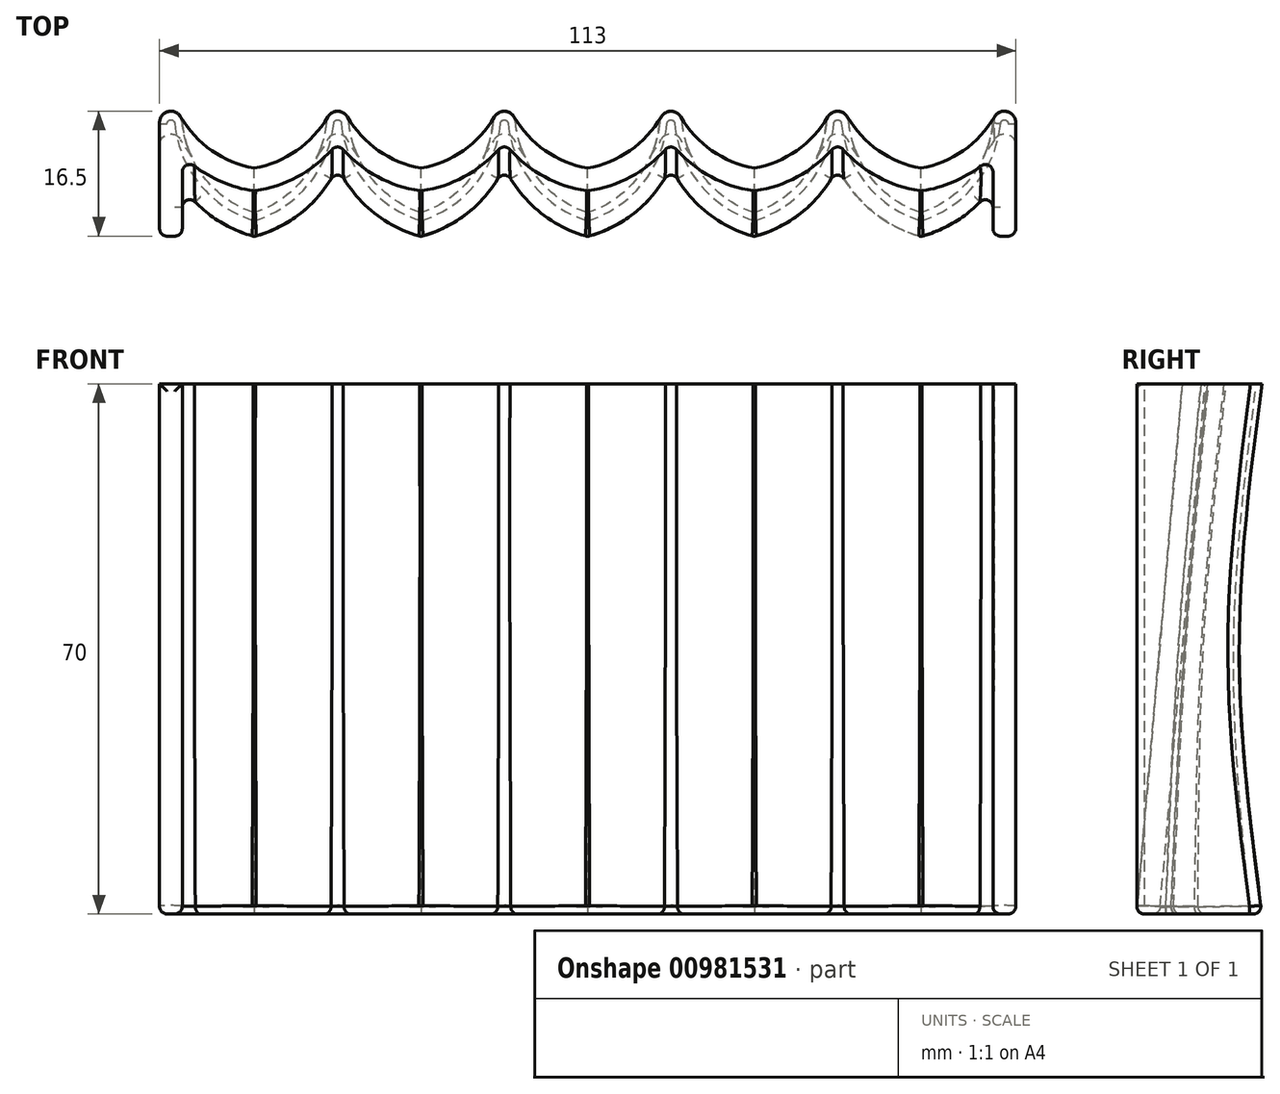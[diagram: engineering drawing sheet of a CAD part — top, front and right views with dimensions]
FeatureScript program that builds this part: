
annotation { "Feature Type Name" : "Feature", "Feature Type Description" : "" }
export const myFeature = defineFeature(function(context is Context, id is Id, definition is map)
    precondition{}
    {
        {
            var Q0;
            Q0=qCreatedBy(makeId("Top.planeOp"),FACE);
            var sketch = newSketch(context, id + "F0", { "sketchPlane" : qUnion([Q0])});
            skLineSegment(sketch, "E0", {"start": v(-56.5, 0) * mm, "end": v(-56.5, 15) * mm});
            skLineSegment(sketch, "E1", {"start": v(56.5, 0) * mm, "end": v(56.5, 15) * mm});
            skArc(sketch, "E2", {"start": v(-53.5, 15.12) * mm, "mid": v(-55.06, 16.5) * mm, "end": v(-56.5, 15) * mm});
            skLineSegment(sketch, "E3", {"start": v(-56.5, 0) * mm, "end": v(-53.5, 0) * mm});
            skLineSegment(sketch, "E4", {"start": v(-53.5, 0) * mm, "end": v(-53.5, 6.56) * mm});
            skLineSegment(sketch, "E5", {"start": v(56.5, 0) * mm, "end": v(53.5, 0) * mm});
            skLineSegment(sketch, "E6", {"start": v(53.5, 0) * mm, "end": v(53.5, 6.56) * mm});
            skLineSegment(sketch, "E7", {"start": v(-33, 3) * mm, "end": v(-11, 3) * mm, "construction": true});
            skLineSegment(sketch, "E8", {"start": v(-11, 3) * mm, "end": v(11, 3) * mm, "construction": true});
            skLineSegment(sketch, "E9", {"start": v(11, 3) * mm, "end": v(33, 3) * mm, "construction": true});
            skLineSegment(sketch, "E10", {"start": v(33, 3) * mm, "end": v(55, 3) * mm, "construction": true});
            skLineSegment(sketch, "E11", {"start": v(-33, 3) * mm, "end": v(-55, 3) * mm, "construction": true});
            skArc(sketch, "E12", {"start": v(56.5, 15) * mm, "mid": v(55, 16.5) * mm, "end": v(53.5, 15) * mm});
            skArc(sketch, "E13", {"start": v(-53.5, 15.12) * mm, "mid": v(-50.57, 7.64) * mm, "end": v(-44, 3) * mm});
            skArc(sketch, "E14", {"start": v(-31.5, 15.12) * mm, "mid": v(-33, 16.5) * mm, "end": v(-34.5, 15.12) * mm});
            skArc(sketch, "E15", {"start": v(-44, 3) * mm, "mid": v(-37.43, 7.64) * mm, "end": v(-34.5, 15.12) * mm});
            skLineSegment(sketch, "E16", {"start": v(0, 0) * mm, "end": v(0, 3) * mm, "construction": true});
            skArc(sketch, "E17", {"start": v(-31.5, 15.12) * mm, "mid": v(-28.57, 7.64) * mm, "end": v(-22, 3) * mm});
            skArc(sketch, "E18", {"start": v(-9.5, 15.12) * mm, "mid": v(-11, 16.5) * mm, "end": v(-12.5, 15.12) * mm});
            skArc(sketch, "E19", {"start": v(-22, 3) * mm, "mid": v(-15.43, 7.64) * mm, "end": v(-12.5, 15.12) * mm});
            skArc(sketch, "E20", {"start": v(-9.5, 15.12) * mm, "mid": v(-6.57, 7.64) * mm, "end": v(0, 3) * mm});
            skArc(sketch, "E21", {"start": v(0, 3) * mm, "mid": v(6.57, 7.64) * mm, "end": v(9.5, 15.12) * mm});
            skArc(sketch, "E22", {"start": v(12.5, 15.12) * mm, "mid": v(11, 16.5) * mm, "end": v(9.5, 15.12) * mm});
            skArc(sketch, "E23", {"start": v(12.5, 15.12) * mm, "mid": v(15.43, 7.64) * mm, "end": v(22, 3) * mm});
            skArc(sketch, "E24", {"start": v(22, 3) * mm, "mid": v(28.57, 7.64) * mm, "end": v(31.5, 15.12) * mm});
            skArc(sketch, "E25", {"start": v(34.5, 15.12) * mm, "mid": v(33, 16.5) * mm, "end": v(31.5, 15.12) * mm});
            skArc(sketch, "E26", {"start": v(34.5, 15.12) * mm, "mid": v(37.43, 7.64) * mm, "end": v(44, 3) * mm});
            skArc(sketch, "E27", {"start": v(44, 3) * mm, "mid": v(50.53, 7.59) * mm, "end": v(53.5, 15) * mm});
            skArc(sketch, "E28.0", {"start": v(44, -0.13) * mm, "mid": v(49.34, 2.37) * mm, "end": v(53.5, 6.56) * mm});
            skArc(sketch, "E28.1", {"start": v(33, 9.18) * mm, "mid": v(37.46, 3.3) * mm, "end": v(44, -0.13) * mm});
            skArc(sketch, "E28.2", {"start": v(22, -0.13) * mm, "mid": v(28.54, 3.3) * mm, "end": v(33, 9.18) * mm});
            skArc(sketch, "E28.3", {"start": v(11, 9.18) * mm, "mid": v(15.46, 3.3) * mm, "end": v(22, -0.13) * mm});
            skArc(sketch, "E28.4", {"start": v(0, -0.13) * mm, "mid": v(6.54, 3.3) * mm, "end": v(11, 9.18) * mm});
            skArc(sketch, "E28.5", {"start": v(-11, 9.18) * mm, "mid": v(-6.54, 3.3) * mm, "end": v(0, -0.13) * mm});
            skArc(sketch, "E28.6", {"start": v(-53.5, 6.56) * mm, "mid": v(-49.34, 2.37) * mm, "end": v(-44, -0.13) * mm});
            skArc(sketch, "E28.7", {"start": v(-44, -0.13) * mm, "mid": v(-37.46, 3.3) * mm, "end": v(-33, 9.18) * mm});
            skArc(sketch, "E28.8", {"start": v(-33, 9.18) * mm, "mid": v(-28.54, 3.3) * mm, "end": v(-22, -0.13) * mm});
            skArc(sketch, "E28.9", {"start": v(-22, -0.13) * mm, "mid": v(-15.46, 3.3) * mm, "end": v(-11, 9.18) * mm});
            skSolve(sketch);
        }
        {
            var Q0;
            Q0=qCreatedBy(makeId("Top.planeOp"),FACE);
            cPlane(context, id + "F1", {"entities" : qUnion([Q0]), "cplaneType" : CPlaneType.OFFSET, "offset" : 70 * mm, "width" : 150 * mm, "height" : 150 * mm});
        }
        {
            var Q0;
            Q0=qCreatedBy(id+"F1.planeOp",FACE);
            var sketch = newSketch(context, id + "F2", { "sketchPlane" : qUnion([Q0])});
            skLineSegment(sketch, "E29.0", {"start": v(-56.5, 0) * mm, "end": v(-53.5, 0) * mm});
            skLineSegment(sketch, "E30.0", {"start": v(56.5, 0) * mm, "end": v(53.5, 0) * mm});
            skLineSegment(sketch, "E31.0", {"start": v(56.5, 0) * mm, "end": v(56.5, 15) * mm});
            skLineSegment(sketch, "E32.0", {"start": v(-56.5, 0) * mm, "end": v(-56.5, 15) * mm});
            skLineSegment(sketch, "E33.0", {"start": v(-33, 3) * mm, "end": v(-55, 3) * mm, "construction": true});
            skLineSegment(sketch, "E34.0", {"start": v(-33, 3) * mm, "end": v(-11, 3) * mm, "construction": true});
            skLineSegment(sketch, "E35.0", {"start": v(-11, 3) * mm, "end": v(11, 3) * mm, "construction": true});
            skLineSegment(sketch, "E36.0", {"start": v(11, 3) * mm, "end": v(33, 3) * mm, "construction": true});
            skLineSegment(sketch, "E37.0", {"start": v(33, 3) * mm, "end": v(55, 3) * mm, "construction": true});
            skArc(sketch, "E38", {"start": v(-53.7, 15.75) * mm, "mid": v(-55.4, 16.45) * mm, "end": v(-56.5, 15) * mm});
            skLineSegment(sketch, "E39", {"start": v(-55, 9) * mm, "end": v(-33, 9) * mm, "construction": true});
            skLineSegment(sketch, "E40", {"start": v(-33, 9) * mm, "end": v(-11, 9) * mm, "construction": true});
            skLineSegment(sketch, "E41", {"start": v(-11, 9) * mm, "end": v(11, 9) * mm, "construction": true});
            skLineSegment(sketch, "E42", {"start": v(11, 9) * mm, "end": v(33, 9) * mm, "construction": true});
            skLineSegment(sketch, "E43", {"start": v(33, 9) * mm, "end": v(55, 9) * mm, "construction": true});
            skArc(sketch, "E44", {"start": v(-53.7, 15.75) * mm, "mid": v(-49.6, 11.3) * mm, "end": v(-44, 9) * mm});
            skArc(sketch, "E45", {"start": v(-44, 9) * mm, "mid": v(-38.4, 11.3) * mm, "end": v(-34.3, 15.75) * mm});
            skArc(sketch, "E46", {"start": v(-31.7, 15.75) * mm, "mid": v(-33, 16.5) * mm, "end": v(-34.3, 15.75) * mm});
            skArc(sketch, "E47", {"start": v(-31.7, 15.75) * mm, "mid": v(-27.6, 11.3) * mm, "end": v(-22, 9) * mm});
            skArc(sketch, "E48", {"start": v(-22, 9) * mm, "mid": v(-16.4, 11.3) * mm, "end": v(-12.3, 15.75) * mm});
            skArc(sketch, "E49", {"start": v(-9.7, 15.75) * mm, "mid": v(-11, 16.5) * mm, "end": v(-12.3, 15.75) * mm});
            skArc(sketch, "E50", {"start": v(-9.7, 15.75) * mm, "mid": v(-5.6, 11.3) * mm, "end": v(0, 9) * mm});
            skArc(sketch, "E51", {"start": v(0, 9) * mm, "mid": v(5.6, 11.3) * mm, "end": v(9.7, 15.75) * mm});
            skArc(sketch, "E52", {"start": v(12.3, 15.75) * mm, "mid": v(11, 16.5) * mm, "end": v(9.7, 15.75) * mm});
            skArc(sketch, "E53", {"start": v(12.3, 15.75) * mm, "mid": v(16.4, 11.3) * mm, "end": v(22, 9) * mm});
            skArc(sketch, "E54", {"start": v(22, 9) * mm, "mid": v(27.6, 11.3) * mm, "end": v(31.7, 15.75) * mm});
            skArc(sketch, "E55", {"start": v(34.3, 15.75) * mm, "mid": v(33, 16.5) * mm, "end": v(31.7, 15.75) * mm});
            skArc(sketch, "E56", {"start": v(34.3, 15.75) * mm, "mid": v(38.4, 11.3) * mm, "end": v(44, 9) * mm});
            skArc(sketch, "E57", {"start": v(44, 9) * mm, "mid": v(49.6, 11.3) * mm, "end": v(53.7, 15.75) * mm});
            skArc(sketch, "E58", {"start": v(56.5, 15) * mm, "mid": v(55.4, 16.45) * mm, "end": v(53.7, 15.75) * mm});
            skArc(sketch, "E59.0", {"start": v(44, 5.96) * mm, "mid": v(49.12, 7.55) * mm, "end": v(53.5, 10.65) * mm});
            skArc(sketch, "E59.1", {"start": v(33, 12.33) * mm, "mid": v(37.88, 8.08) * mm, "end": v(44, 5.96) * mm});
            skArc(sketch, "E59.2", {"start": v(22, 5.96) * mm, "mid": v(28.12, 8.08) * mm, "end": v(33, 12.33) * mm});
            skArc(sketch, "E59.3", {"start": v(11, 12.33) * mm, "mid": v(15.88, 8.08) * mm, "end": v(22, 5.96) * mm});
            skArc(sketch, "E59.4", {"start": v(0, 5.96) * mm, "mid": v(6.12, 8.08) * mm, "end": v(11, 12.33) * mm});
            skArc(sketch, "E59.5", {"start": v(-11, 12.33) * mm, "mid": v(-6.12, 8.08) * mm, "end": v(0, 5.96) * mm});
            skArc(sketch, "E59.6", {"start": v(-53.5, 10.65) * mm, "mid": v(-49.12, 7.55) * mm, "end": v(-44, 5.96) * mm});
            skArc(sketch, "E59.7", {"start": v(-44, 5.96) * mm, "mid": v(-37.88, 8.08) * mm, "end": v(-33, 12.33) * mm});
            skArc(sketch, "E59.8", {"start": v(-33, 12.33) * mm, "mid": v(-28.12, 8.08) * mm, "end": v(-22, 5.96) * mm});
            skArc(sketch, "E59.9", {"start": v(-22, 5.96) * mm, "mid": v(-15.88, 8.08) * mm, "end": v(-11, 12.33) * mm});
            skLineSegment(sketch, "E60", {"start": v(-53.5, 10.65) * mm, "end": v(-53.5, 0) * mm});
            skLineSegment(sketch, "E61", {"start": v(53.5, 10.65) * mm, "end": v(53.5, 0) * mm});
            skSolve(sketch);
        }
        {
            var Q0;
            Q0=qCreatedBy(makeId("Top.planeOp"),FACE);
            cPlane(context, id + "F3", {"entities" : qUnion([Q0]), "cplaneType" : CPlaneType.OFFSET, "offset" : 35 * mm, "width" : 150 * mm, "height" : 150 * mm});
        }
        {
            var Q0;
            Q0=qCreatedBy(id+"F3.planeOp",FACE);
            var sketch = newSketch(context, id + "F4", { "sketchPlane" : qUnion([Q0])});
            skLineSegment(sketch, "E62.0", {"start": v(-33, 3) * mm, "end": v(-55, 3) * mm, "construction": true});
            skLineSegment(sketch, "E63.0", {"start": v(-33, 3) * mm, "end": v(-11, 3) * mm, "construction": true});
            skLineSegment(sketch, "E64.0", {"start": v(-11, 3) * mm, "end": v(11, 3) * mm, "construction": true});
            skLineSegment(sketch, "E65.0", {"start": v(11, 3) * mm, "end": v(33, 3) * mm, "construction": true});
            skLineSegment(sketch, "E66.0", {"start": v(33, 3) * mm, "end": v(55, 3) * mm, "construction": true});
            skLineSegment(sketch, "E67.0", {"start": v(33, 9) * mm, "end": v(55, 9) * mm, "construction": true});
            skLineSegment(sketch, "E68.0", {"start": v(11, 9) * mm, "end": v(33, 9) * mm, "construction": true});
            skLineSegment(sketch, "E69.0", {"start": v(-11, 9) * mm, "end": v(11, 9) * mm, "construction": true});
            skLineSegment(sketch, "E70.0", {"start": v(-33, 9) * mm, "end": v(-11, 9) * mm, "construction": true});
            skLineSegment(sketch, "E71.0", {"start": v(-55, 9) * mm, "end": v(-33, 9) * mm, "construction": true});
            skLineSegment(sketch, "E72.0", {"start": v(-56.5, 0) * mm, "end": v(-53.5, 0) * mm});
            skLineSegment(sketch, "E73.0", {"start": v(-56.5, 0) * mm, "end": v(-56.5, 15) * mm, "construction": true});
            skLineSegment(sketch, "E74.0", {"start": v(56.5, 0) * mm, "end": v(53.5, 0) * mm});
            skLineSegment(sketch, "E75.0", {"start": v(56.5, 0) * mm, "end": v(56.5, 15) * mm, "construction": true});
            skLineSegment(sketch, "E76", {"start": v(-55, 6) * mm, "end": v(-33, 6) * mm, "construction": true});
            skLineSegment(sketch, "E77", {"start": v(-33, 6) * mm, "end": v(-11, 6) * mm, "construction": true});
            skLineSegment(sketch, "E78", {"start": v(-11, 6) * mm, "end": v(11, 6) * mm, "construction": true});
            skLineSegment(sketch, "E79", {"start": v(11, 6) * mm, "end": v(33, 6) * mm, "construction": true});
            skLineSegment(sketch, "E80", {"start": v(33, 6) * mm, "end": v(55, 6) * mm, "construction": true});
            skLineSegment(sketch, "E81", {"start": v(-56.5, 0) * mm, "end": v(-56.5, 12) * mm});
            skLineSegment(sketch, "E82", {"start": v(56.5, 0) * mm, "end": v(56.5, 12) * mm});
            skArc(sketch, "E83", {"start": v(-53.7, 12.75) * mm, "mid": v(-55.4, 13.45) * mm, "end": v(-56.5, 12) * mm});
            skArc(sketch, "E84", {"start": v(-53.7, 12.75) * mm, "mid": v(-49.6, 8.3) * mm, "end": v(-44, 6) * mm});
            skArc(sketch, "E85", {"start": v(-44, 6) * mm, "mid": v(-38.4, 8.3) * mm, "end": v(-34.3, 12.75) * mm});
            skArc(sketch, "E86", {"start": v(-31.7, 12.75) * mm, "mid": v(-33, 13.5) * mm, "end": v(-34.3, 12.75) * mm});
            skArc(sketch, "E87", {"start": v(-31.7, 12.75) * mm, "mid": v(-27.6, 8.3) * mm, "end": v(-22, 6) * mm});
            skArc(sketch, "E88", {"start": v(-22, 6) * mm, "mid": v(-16.4, 8.3) * mm, "end": v(-12.3, 12.75) * mm});
            skArc(sketch, "E89", {"start": v(-9.7, 12.75) * mm, "mid": v(-11, 13.5) * mm, "end": v(-12.3, 12.75) * mm});
            skArc(sketch, "E90", {"start": v(-9.7, 12.75) * mm, "mid": v(-5.6, 8.3) * mm, "end": v(0, 6) * mm});
            skArc(sketch, "E91", {"start": v(0, 6) * mm, "mid": v(5.6, 8.3) * mm, "end": v(9.7, 12.75) * mm});
            skArc(sketch, "E92", {"start": v(12.3, 12.75) * mm, "mid": v(11, 13.5) * mm, "end": v(9.7, 12.75) * mm});
            skArc(sketch, "E93", {"start": v(12.3, 12.75) * mm, "mid": v(16.4, 8.3) * mm, "end": v(22, 6) * mm});
            skArc(sketch, "E94", {"start": v(22, 6) * mm, "mid": v(27.6, 8.3) * mm, "end": v(31.7, 12.75) * mm});
            skArc(sketch, "E95", {"start": v(34.3, 12.75) * mm, "mid": v(33, 13.5) * mm, "end": v(31.7, 12.75) * mm});
            skArc(sketch, "E96", {"start": v(34.3, 12.75) * mm, "mid": v(38.4, 8.3) * mm, "end": v(44, 6) * mm});
            skArc(sketch, "E97", {"start": v(44, 6) * mm, "mid": v(49.6, 8.3) * mm, "end": v(53.7, 12.75) * mm});
            skLineSegment(sketch, "E98", {"start": v(53.5, 7.65) * mm, "end": v(53.5, 0) * mm});
            skLineSegment(sketch, "E99", {"start": v(-53.5, 7.65) * mm, "end": v(-53.5, 0) * mm});
            skLineSegment(sketch, "E100", {"start": v(0, 6) * mm, "end": v(0, 3) * mm, "construction": true});
            skLineSegment(sketch, "E101", {"start": v(0, 3) * mm, "end": v(0, 6) * mm, "construction": true});
            skLineSegment(sketch, "E102", {"start": v(0, 6) * mm, "end": v(0, 9) * mm, "construction": true});
            skArc(sketch, "E103", {"start": v(56.5, 12) * mm, "mid": v(55.4, 13.45) * mm, "end": v(53.7, 12.75) * mm});
            skArc(sketch, "E104.0", {"start": v(44, 2.96) * mm, "mid": v(49.12, 4.55) * mm, "end": v(53.5, 7.65) * mm});
            skArc(sketch, "E104.1", {"start": v(33, 9.33) * mm, "mid": v(37.88, 5.08) * mm, "end": v(44, 2.96) * mm});
            skArc(sketch, "E104.2", {"start": v(22, 2.96) * mm, "mid": v(28.12, 5.08) * mm, "end": v(33, 9.33) * mm});
            skArc(sketch, "E104.3", {"start": v(11, 9.33) * mm, "mid": v(15.88, 5.08) * mm, "end": v(22, 2.96) * mm});
            skArc(sketch, "E104.4", {"start": v(0, 2.96) * mm, "mid": v(6.12, 5.08) * mm, "end": v(11, 9.33) * mm});
            skArc(sketch, "E104.5", {"start": v(-11, 9.33) * mm, "mid": v(-6.12, 5.08) * mm, "end": v(0, 2.96) * mm});
            skArc(sketch, "E104.6", {"start": v(-53.5, 7.65) * mm, "mid": v(-49.12, 4.55) * mm, "end": v(-44, 2.96) * mm});
            skArc(sketch, "E104.7", {"start": v(-44, 2.96) * mm, "mid": v(-37.88, 5.08) * mm, "end": v(-33, 9.33) * mm});
            skArc(sketch, "E104.8", {"start": v(-33, 9.33) * mm, "mid": v(-28.12, 5.08) * mm, "end": v(-22, 2.96) * mm});
            skArc(sketch, "E104.9", {"start": v(-22, 2.96) * mm, "mid": v(-15.88, 5.08) * mm, "end": v(-11, 9.33) * mm});
            skSolve(sketch);
        }
        {
            var Q0;
            Q0 = qSketchRegion(id + "F0", true);
            var Q1;
            Q1 = qSketchRegion(id + "F4", true);
            var Q2;
            Q2 = qSketchRegion(id + "F2", true);
            loft(context, id + "F5", {"sheetProfilesArray" : [{ "sheetProfileEntities" : qUnion([Q0]) }, { "sheetProfileEntities" : qUnion([Q1]) }, { "sheetProfileEntities" : qUnion([Q2]) }]});
        }
        {
            var Q0;
            Q0=makeQuery(id+"F5.opLoft","CAP_FACE",FACE,{"disambiguationData":[OSD([makeQuery(id+"F0.imprint","IMPRINT",FACE,{"disambiguationData":[TD([[makeQuery(id+"F0.imprint","IMPRINT",EDGE,{"derivedFrom":sQuery(id+"F0.wireOp",EDGE,"E0")}),-1.0]])]})])],"isStart":true});
            var Q1;
            Q1=makeQuery(id+"F5.opLoft","SWEPT_EDGE",EDGE,{"disambiguationData":[OSD([sQuery(id+"F0.wireOp",EDGE,"E28.0"),sQuery(id+"F0.wireOp",EDGE,"E28.1"),sQuery(id+"F2.wireOp",EDGE,"E59.0"),sQuery(id+"F2.wireOp",EDGE,"E59.1"),sQuery(id+"F4.wireOp",EDGE,"f05942cf-1fd4-4216-8ab5-6da0ba2a5f30.0"),sQuery(id+"F4.wireOp",EDGE,"f05942cf-1fd4-4216-8ab5-6da0ba2a5f30.1")])]});
            var Q2;
            Q2=makeQuery(id+"F5.opLoft","SWEPT_EDGE",EDGE,{"disambiguationData":[OSD([sQuery(id+"F0.wireOp",EDGE,"E28.4"),sQuery(id+"F0.wireOp",EDGE,"E28.5"),sQuery(id+"F2.wireOp",EDGE,"E59.4"),sQuery(id+"F2.wireOp",EDGE,"E59.5"),sQuery(id+"F4.wireOp",EDGE,"f05942cf-1fd4-4216-8ab5-6da0ba2a5f30.4"),sQuery(id+"F4.wireOp",EDGE,"f05942cf-1fd4-4216-8ab5-6da0ba2a5f30.5")])]});
            var Q3;
            Q3=makeQuery(id+"F5.opLoft","SWEPT_EDGE",EDGE,{"disambiguationData":[OSD([sQuery(id+"F0.wireOp",EDGE,"E28.8"),sQuery(id+"F0.wireOp",EDGE,"E28.9"),sQuery(id+"F2.wireOp",EDGE,"E59.8"),sQuery(id+"F2.wireOp",EDGE,"E59.9"),sQuery(id+"F4.wireOp",EDGE,"f05942cf-1fd4-4216-8ab5-6da0ba2a5f30.8"),sQuery(id+"F4.wireOp",EDGE,"f05942cf-1fd4-4216-8ab5-6da0ba2a5f30.9")])]});
            var Q4;
            Q4=makeQuery(id+"F5.opLoft","SWEPT_EDGE",EDGE,{"disambiguationData":[OSD([sQuery(id+"F0.wireOp",EDGE,"E28.6"),sQuery(id+"F0.wireOp",EDGE,"E28.7"),sQuery(id+"F2.wireOp",EDGE,"E59.6"),sQuery(id+"F2.wireOp",EDGE,"E59.7"),sQuery(id+"F4.wireOp",EDGE,"f05942cf-1fd4-4216-8ab5-6da0ba2a5f30.6"),sQuery(id+"F4.wireOp",EDGE,"f05942cf-1fd4-4216-8ab5-6da0ba2a5f30.7")])]});
            var Q5;
            Q5=makeQuery(id+"F5.opLoft","SWEPT_FACE",FACE,{"disambiguationData":[OSD([sQuery(id+"F0.wireOp",EDGE,"E0"),sQuery(id+"F0.wireOp",EDGE,"E3"),sQuery(id+"F0.wireOp",EDGE,"E4"),sQuery(id+"F2.wireOp",EDGE,"E29.0"),sQuery(id+"F2.wireOp",EDGE,"E32.0"),sQuery(id+"F2.wireOp",EDGE,"E60"),sQuery(id+"F4.wireOp",EDGE,"E72.0"),sQuery(id+"F4.wireOp",EDGE,"E81"),sQuery(id+"F4.wireOp",EDGE,"E99")])]});
            var Q6;
            Q6=makeQuery(id+"F5.opLoft","SWEPT_EDGE",EDGE,{"disambiguationData":[OSD([sQuery(id+"F0.wireOp",EDGE,"E0"),sQuery(id+"F0.wireOp",EDGE,"E3"),sQuery(id+"F2.wireOp",EDGE,"E29.0"),sQuery(id+"F2.wireOp",EDGE,"E32.0"),sQuery(id+"F4.wireOp",EDGE,"E72.0"),sQuery(id+"F4.wireOp",EDGE,"E81")])]});
            var Q7;
            Q7=makeQuery(id+"F5.opLoft","SWEPT_EDGE",EDGE,{"disambiguationData":[OSD([sQuery(id+"F0.wireOp",EDGE,"E1"),sQuery(id+"F0.wireOp",EDGE,"E5"),sQuery(id+"F2.wireOp",EDGE,"E30.0"),sQuery(id+"F2.wireOp",EDGE,"E31.0"),sQuery(id+"F4.wireOp",EDGE,"E74.0"),sQuery(id+"F4.wireOp",EDGE,"E82")])]});
            var Q8;
            Q8=makeQuery(id+"F5.opLoft","SWEPT_EDGE",EDGE,{"disambiguationData":[OSD([sQuery(id+"F0.wireOp",EDGE,"E5"),sQuery(id+"F0.wireOp",EDGE,"E6"),sQuery(id+"F2.wireOp",EDGE,"E30.0"),sQuery(id+"F2.wireOp",EDGE,"E61"),sQuery(id+"F4.wireOp",EDGE,"E74.0"),sQuery(id+"F4.wireOp",EDGE,"E98")])]});
            var Q9;
            Q9=makeQuery(id+"F5.opLoft","SWEPT_EDGE",EDGE,{"disambiguationData":[OSD([sQuery(id+"F0.wireOp",EDGE,"E28.2"),sQuery(id+"F0.wireOp",EDGE,"E28.3"),sQuery(id+"F2.wireOp",EDGE,"E59.2"),sQuery(id+"F2.wireOp",EDGE,"E59.3"),sQuery(id+"F4.wireOp",EDGE,"f05942cf-1fd4-4216-8ab5-6da0ba2a5f30.2"),sQuery(id+"F4.wireOp",EDGE,"f05942cf-1fd4-4216-8ab5-6da0ba2a5f30.3")])]});
            var Q10;
            Q10=makeQuery(id+"F5.opLoft","SWEPT_EDGE",EDGE,{"disambiguationData":[OSD([sQuery(id+"F0.wireOp",EDGE,"E6"),sQuery(id+"F0.wireOp",EDGE,"E28.0"),sQuery(id+"F2.wireOp",EDGE,"E59.0"),sQuery(id+"F2.wireOp",EDGE,"E61"),sQuery(id+"F4.wireOp",EDGE,"E98"),sQuery(id+"F4.wireOp",EDGE,"E104.0")])]});
            var Q11;
            Q11=makeQuery(id+"F5.opLoft","SWEPT_EDGE",EDGE,{"disambiguationData":[OSD([sQuery(id+"F0.wireOp",EDGE,"E4"),sQuery(id+"F0.wireOp",EDGE,"E28.6"),sQuery(id+"F2.wireOp",EDGE,"E59.6"),sQuery(id+"F2.wireOp",EDGE,"E60"),sQuery(id+"F4.wireOp",EDGE,"E99"),sQuery(id+"F4.wireOp",EDGE,"E104.6")])]});
            var Q12;
            Q12=makeQuery(id+"F5.opLoft","SWEPT_EDGE",EDGE,{"disambiguationData":[OSD([sQuery(id+"F0.wireOp",EDGE,"E28.7"),sQuery(id+"F0.wireOp",EDGE,"E28.8"),sQuery(id+"F2.wireOp",EDGE,"E59.7"),sQuery(id+"F2.wireOp",EDGE,"E59.8"),sQuery(id+"F4.wireOp",EDGE,"E104.7"),sQuery(id+"F4.wireOp",EDGE,"E104.8")])]});
            var Q13;
            Q13=makeQuery(id+"F5.opLoft","SWEPT_EDGE",EDGE,{"disambiguationData":[OSD([sQuery(id+"F0.wireOp",EDGE,"E28.5"),sQuery(id+"F0.wireOp",EDGE,"E28.9"),sQuery(id+"F2.wireOp",EDGE,"E59.5"),sQuery(id+"F2.wireOp",EDGE,"E59.9"),sQuery(id+"F4.wireOp",EDGE,"E104.5"),sQuery(id+"F4.wireOp",EDGE,"E104.9")])]});
            var Q14;
            Q14=makeQuery(id+"F5.opLoft","SWEPT_EDGE",EDGE,{"disambiguationData":[OSD([sQuery(id+"F0.wireOp",EDGE,"E28.3"),sQuery(id+"F0.wireOp",EDGE,"E28.4"),sQuery(id+"F2.wireOp",EDGE,"E59.3"),sQuery(id+"F2.wireOp",EDGE,"E59.4"),sQuery(id+"F4.wireOp",EDGE,"E104.3"),sQuery(id+"F4.wireOp",EDGE,"E104.4")])]});
            var Q15;
            Q15=makeQuery(id+"F5.opLoft","SWEPT_EDGE",EDGE,{"disambiguationData":[OSD([sQuery(id+"F0.wireOp",EDGE,"E28.1"),sQuery(id+"F0.wireOp",EDGE,"E28.2"),sQuery(id+"F2.wireOp",EDGE,"E59.1"),sQuery(id+"F2.wireOp",EDGE,"E59.2"),sQuery(id+"F4.wireOp",EDGE,"E104.1"),sQuery(id+"F4.wireOp",EDGE,"E104.2")])]});
            fillet(context, id + "F6", {"entities" : qUnion([Q0, Q1, Q2, Q3, Q4, Q5, Q6, Q7, Q8, Q9, Q10, Q11, Q12, Q13, Q14, Q15]), "radius" : 1 * mm, "tangentPropagation" : true, "allowEdgeOverflow" : false});
        }
    });
